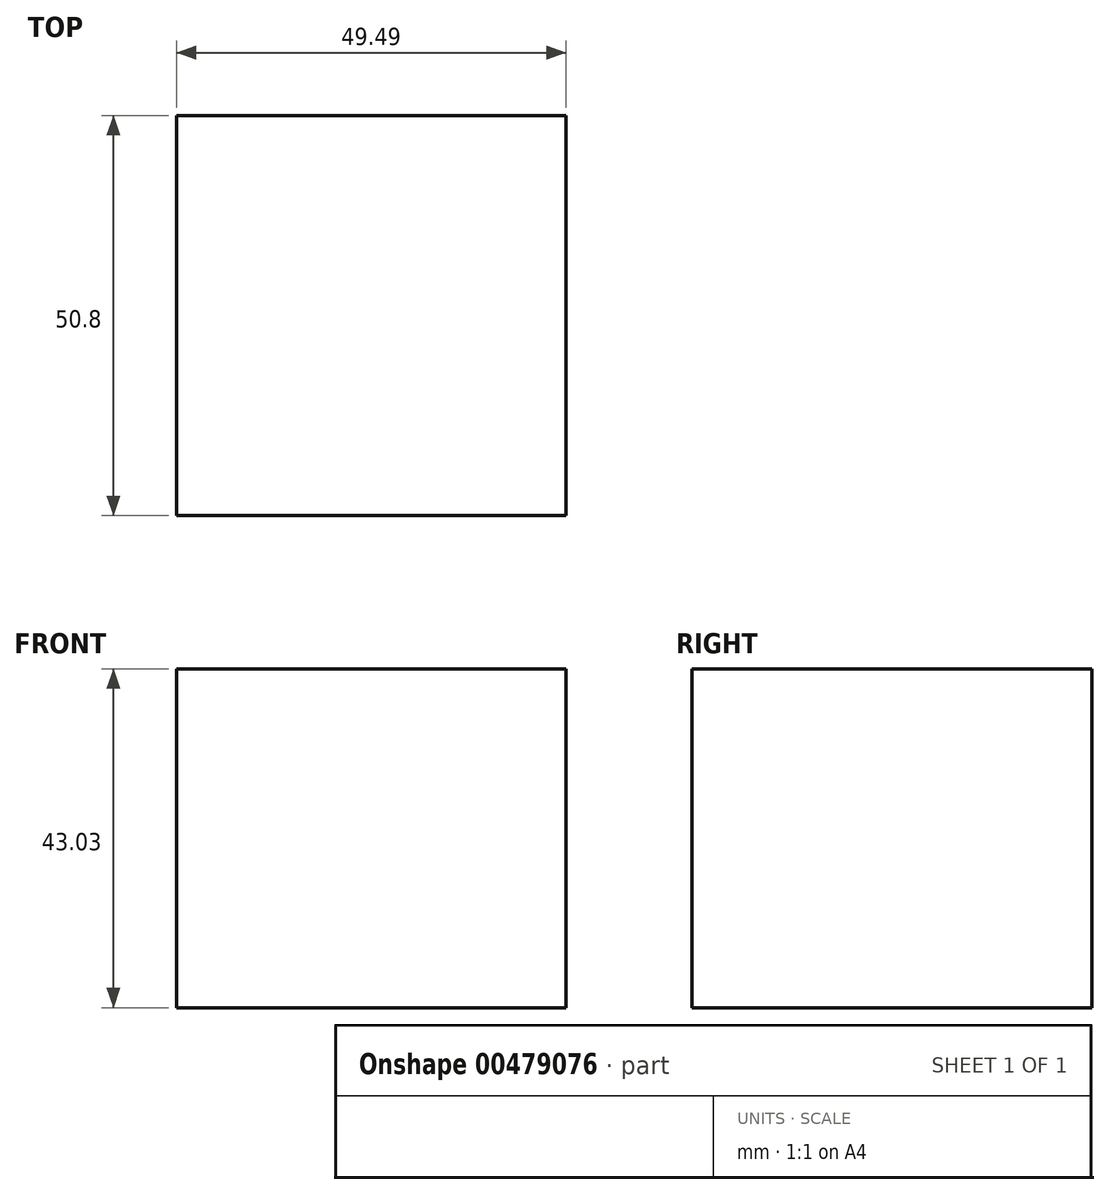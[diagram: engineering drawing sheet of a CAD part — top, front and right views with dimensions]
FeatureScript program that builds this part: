
annotation { "Feature Type Name" : "Feature", "Feature Type Description" : "" }
export const myFeature = defineFeature(function(context is Context, id is Id, definition is map)
    precondition{}
    {
        {
            var Q0;
            Q0=qCreatedBy(makeId("Front.planeOp"),FACE);
            var sketch = newSketch(context, id + "F0", { "sketchPlane" : qUnion([Q0])});
            skLineSegment(sketch, "E0.bottom", {"start": v(0, 0) * mm, "end": v(49.5, 0) * mm});
            skLineSegment(sketch, "E0.top", {"start": v(0, 43.03) * mm, "end": v(49.5, 43.03) * mm});
            skLineSegment(sketch, "E0.left", {"start": v(0, 0) * mm, "end": v(0, 43.03) * mm});
            skLineSegment(sketch, "E0.right", {"start": v(49.5, 0) * mm, "end": v(49.5, 43.03) * mm});
            skSolve(sketch);
        }
        {
            var Q0;
            Q0=makeQuery(id+"F0.imprint","IMPRINT",FACE,{"disambiguationData":[TD([[makeQuery(id+"F0.imprint","IMPRINT",EDGE,{"derivedFrom":sQuery(id+"F0.wireOp",EDGE,"E0.bottom")}),1.0]])]});
            extrude(context, id + "F1", {"entities" : qUnion([Q0]), "oppositeDirection" : true, "depth" : 50.8 * mm});
        }
    });
